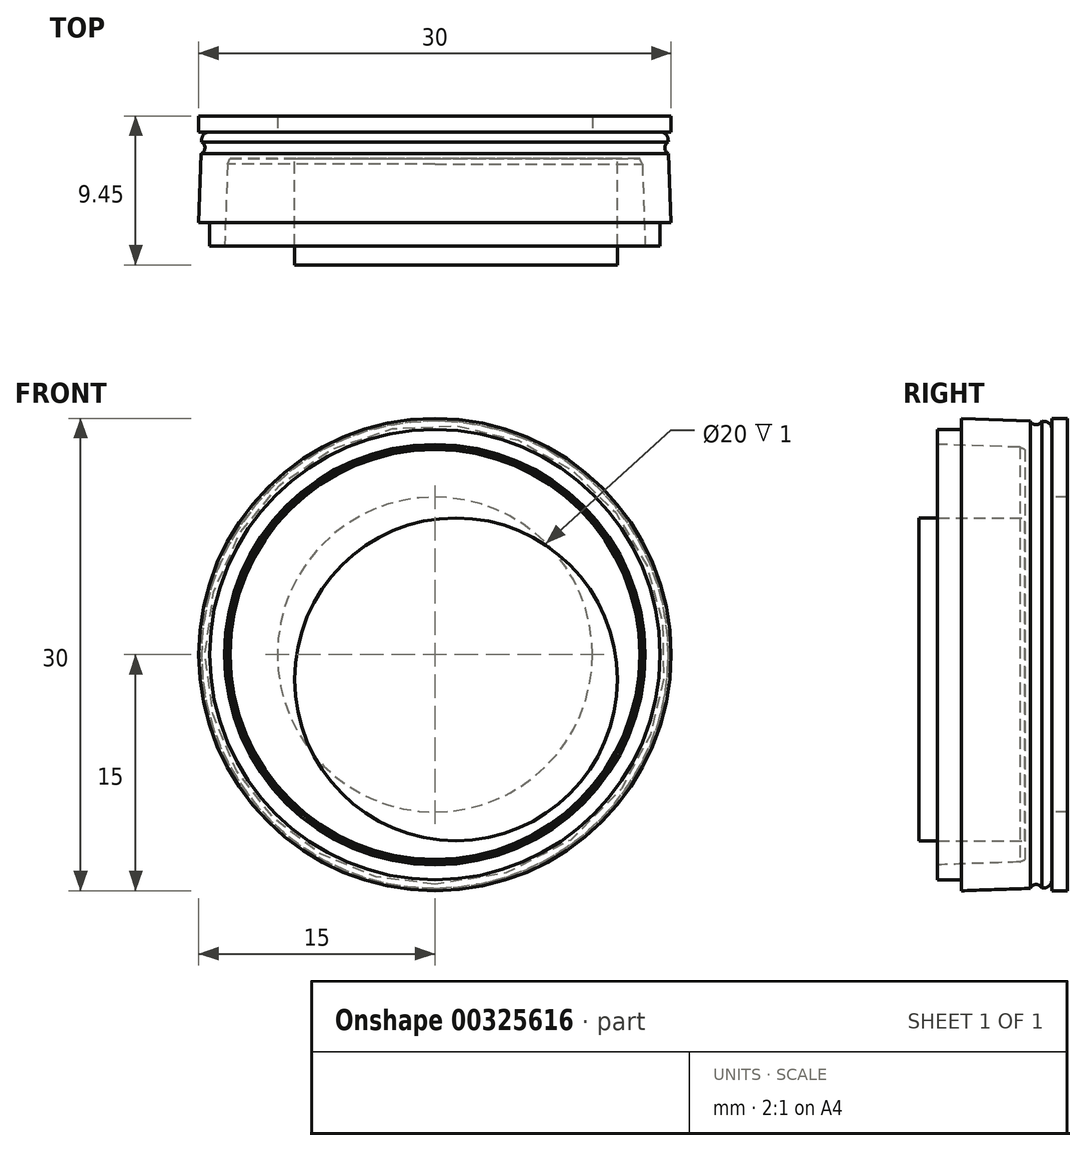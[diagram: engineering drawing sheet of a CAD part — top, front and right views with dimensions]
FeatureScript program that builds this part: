
annotation { "Feature Type Name" : "Feature", "Feature Type Description" : "" }
export const myFeature = defineFeature(function(context is Context, id is Id, definition is map)
    precondition{}
    {
        {
            var Q0;
            Q0=qCreatedBy(makeId("Front.planeOp"),FACE);
            var sketch = newSketch(context, id + "F0", { "sketchPlane" : qUnion([Q0])});
            skCircle(sketch, "E0", {"center": v(0, 0) * mm, "radius": 14.8 * mm});
            skSolve(sketch);
        }
        {
            var Q0;
            Q0 = qSketchRegion(id + "F0", true);
            extrude(context, id + "F1", {"entities" : qUnion([Q0]), "depth" : 7.25 * mm, "hasDraft" : true, "draftAngle" : 2 * degree});
        }
        {
            var Q0;
            Q0=qCreatedBy(makeId("Right.planeOp"),FACE);
            var sketch = newSketch(context, id + "F2", { "sketchPlane" : qUnion([Q0])});
            skLineSegment(sketch, "E1", {"start": v(-11.9, 0) * mm, "end": v(5.19, 0) * mm});
            skCircle(sketch, "E2", {"center": v(-1, -15) * mm, "radius": 0.4 * mm});
            skSolve(sketch);
        }
        {
            var Q0;
            Q0=makeQuery(id+"F2.imprint","IMPRINT",FACE,{"disambiguationData":[TD([[makeQuery(id+"F2.imprint","IMPRINT",EDGE,{"derivedFrom":sQuery(id+"F2.wireOp",EDGE,"E2")}),1.0]])]});
            var Q1;
            Q1=sQuery(id+"F2.wireOp",EDGE,"E1");
            revolve(context, id + "F3", {"operationType" : NewBodyOperationType.REMOVE, "entities" : qUnion([Q0]), "axis" : qUnion([Q1]), "revolveType" : RevolveType.FULL, "oppositeDirection" : true});
        }
        {
            var Q0;
            Q0=makeQuery(id+"F1.opExtrude","CAP_FACE",FACE,{"disambiguationData":[OSD([sQuery(id+"F0.wireOp",EDGE,"E0")])],"isStart":false});
            shell(context, id + "F4", {"entities" : qUnion([Q0]), "thickness" : 1.7 * mm});
        }
        {
            var Q0;
            Q0=makeQuery(id+"F1.opExtrude","CAP_EDGE",EDGE,{"disambiguationData":[OSD([sQuery(id+"F0.wireOp",EDGE,"E0")])],"isStart":true});
            fillet(context, id + "F5", {"entities" : qUnion([Q0]), "radius" : .5 * mm, "tangentPropagation" : true, "allowEdgeOverflow" : false});
        }
        {
            var Q0;
            Q0=makeQuery(id+"F1.opExtrude","CAP_FACE",FACE,{"disambiguationData":[OSD([sQuery(id+"F0.wireOp",EDGE,"E0")])],"isStart":false});
            var sketch = newSketch(context, id + "F6", { "sketchPlane" : qUnion([Q0])});
            skCircle(sketch, "E3", {"center": v(0, 0) * mm, "radius": 14.3 * mm});
            skSolve(sketch);
        }
        {
            var Q0;
            Q0=makeQuery(id+"F6.imprint","IMPRINT",FACE,{"disambiguationData":[TD([[makeQuery(id+"F6.imprint","IMPRINT",EDGE,{"derivedFrom":sQuery(id+"F6.wireOp",EDGE,"E3")}),-1.0]])]});
            extrude(context, id + "F7", {"entities" : qUnion([Q0]), "operationType" : NewBodyOperationType.REMOVE, "oppositeDirection" : true, "depth" : 1.5 * mm});
        }
        {
            var Q0;
            Q0=makeQuery(id+"F1.opExtrude","CAP_FACE",FACE,{"disambiguationData":[OSD([sQuery(id+"F0.wireOp",EDGE,"E0")])],"isStart":true});
            var sketch = newSketch(context, id + "F8", { "sketchPlane" : qUnion([Q0])});
            skCircle(sketch, "E4", {"center": v(0, 0) * mm, "radius": 15 * mm});
            skCircle(sketch, "E5", {"center": v(0, 0) * mm, "radius": 10 * mm});
            skSolve(sketch);
        }
        {
            var Q0;
            Q0 = qSketchRegion(id + "F8", true);
            extrude(context, id + "F9", {"entities" : qUnion([Q0]), "depth" : 1 * mm});
        }
        {
            var Q0;
            {var subQ0=sQuery(id+"F0.wireOp",EDGE,"E0");Q0=makeQuery(id+"F4.opShell","OFFSET_FACE",FACE,{"disambiguationData":[OSD([subQ0]),TDD([makeQuery(id+"F1.opExtrude","CAP_FACE",FACE,{"disambiguationData":[OSD([subQ0])],"isStart":true})])]});}
            var sketch = newSketch(context, id + "F10", { "sketchPlane" : qUnion([Q0])});
            skCircle(sketch, "E6", {"center": v(1.34, -1.57) * mm, "radius": 10.25 * mm});
            skSolve(sketch);
        }
        {
            var Q0;
            Q0=makeQuery(id+"F10.imprint","IMPRINT",FACE,{"disambiguationData":[TD([[makeQuery(id+"F10.imprint","IMPRINT",EDGE,{"derivedFrom":sQuery(id+"F10.wireOp",EDGE,"E6")}),1.0]])]});
            extrude(context, id + "F11", {"entities" : qUnion([Q0]), "depth" : 6.75 * mm});
        }
    });
